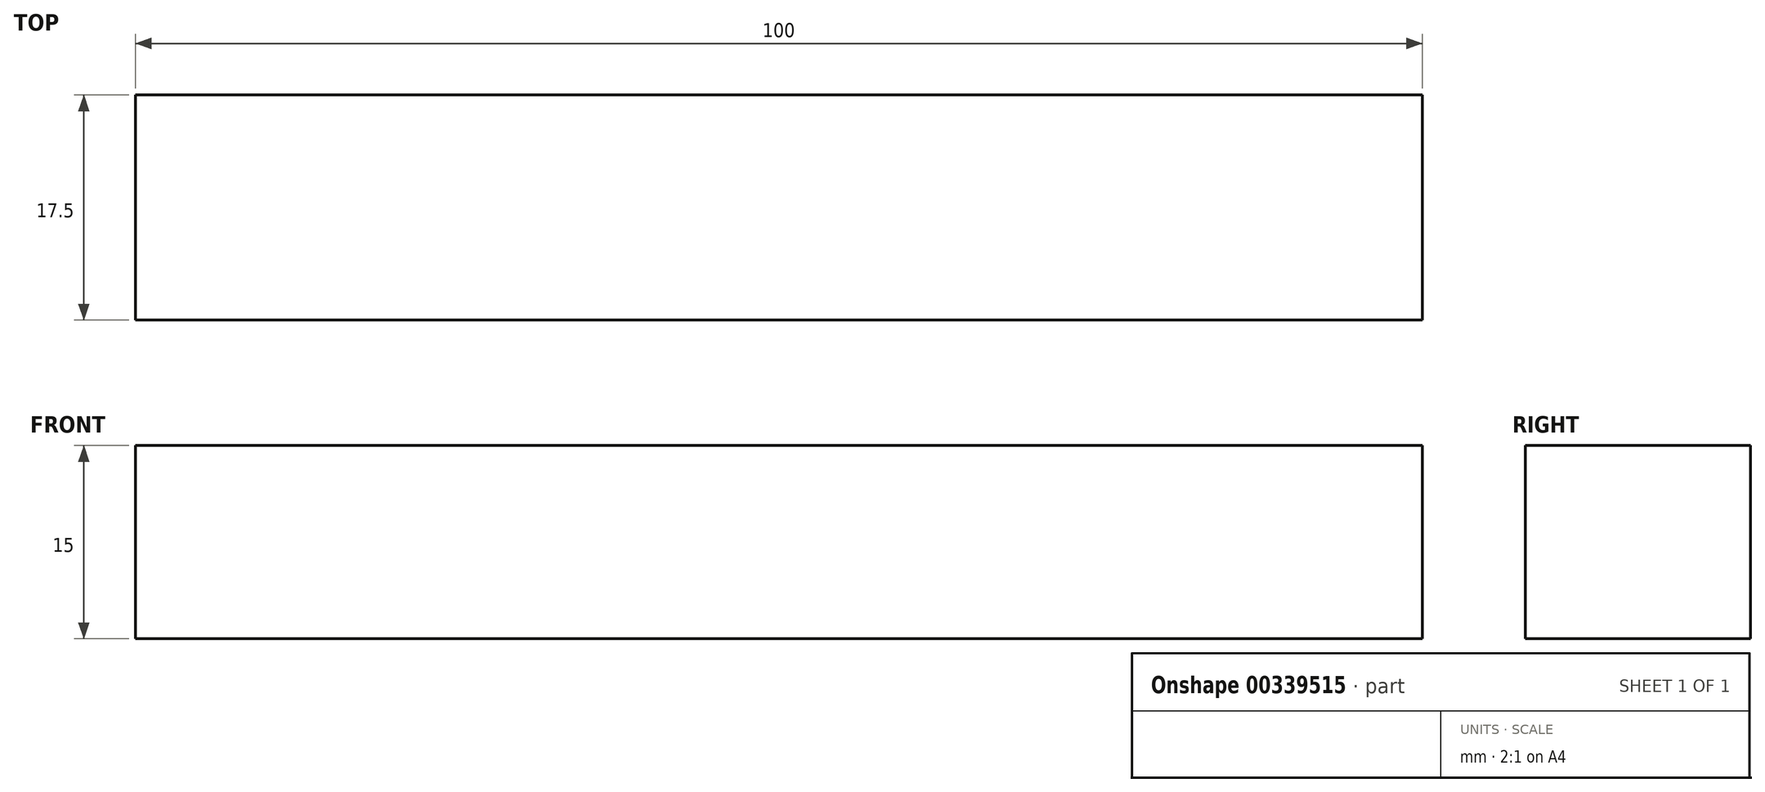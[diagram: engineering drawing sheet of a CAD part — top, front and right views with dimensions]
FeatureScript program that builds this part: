
annotation { "Feature Type Name" : "Feature", "Feature Type Description" : "" }
export const myFeature = defineFeature(function(context is Context, id is Id, definition is map)
    precondition{}
    {
        {
            var Q0;
            Q0=qCreatedBy(makeId("Right.planeOp"),FACE);
            var sketch = newSketch(context, id + "F0", { "sketchPlane" : qUnion([Q0])});
            skLineSegment(sketch, "E0.bottom", {"start": v(8.75, -7.5) * mm, "end": v(-8.75, -7.5) * mm});
            skLineSegment(sketch, "E0.top", {"start": v(8.75, 7.5) * mm, "end": v(-8.75, 7.5) * mm});
            skLineSegment(sketch, "E0.left", {"start": v(8.75, -7.5) * mm, "end": v(8.75, 7.5) * mm});
            skLineSegment(sketch, "E0.right", {"start": v(-8.75, -7.5) * mm, "end": v(-8.75, 7.5) * mm});
            skPoint(sketch, "E0.middle", {"position": v(0, 0) * mm});
            skSolve(sketch);
        }
        {
            var Q0;
            Q0 = qSketchRegion(id + "F0", true);
            extrude(context, id + "F1", {"entities" : qUnion([Q0]), "depth" : 100 * mm});
        }
    });
